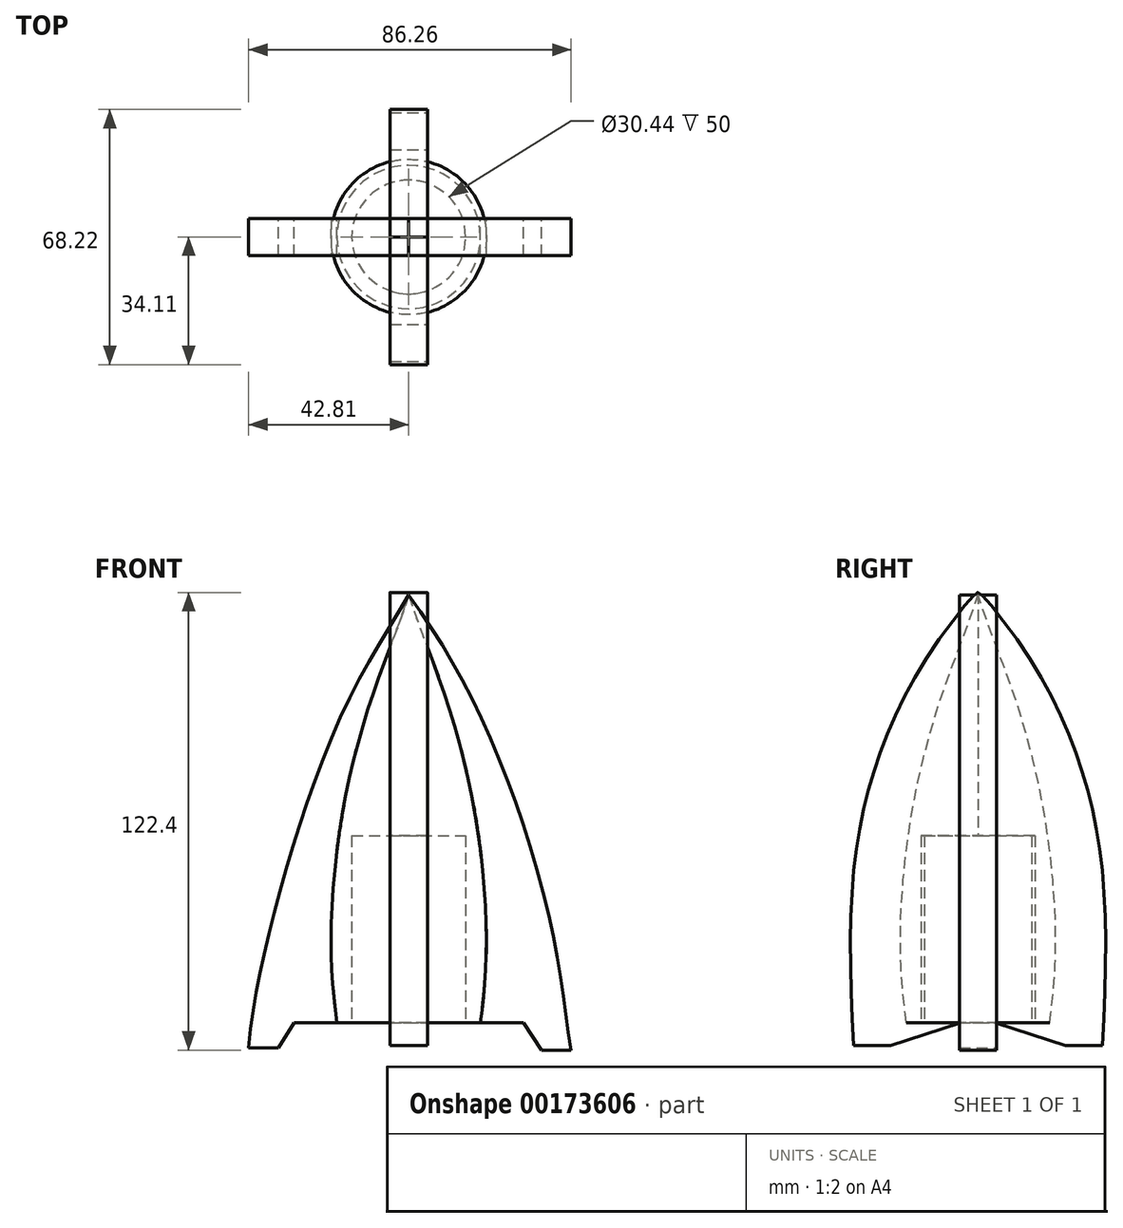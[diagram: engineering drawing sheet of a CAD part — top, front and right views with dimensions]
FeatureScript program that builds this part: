
annotation { "Feature Type Name" : "Feature", "Feature Type Description" : "" }
export const myFeature = defineFeature(function(context is Context, id is Id, definition is map)
    precondition{}
    {
        {
            var Q0;
            Q0=qCreatedBy(makeId("Front.planeOp"),FACE);
            var sketch = newSketch(context, id + "F0", { "sketchPlane" : qUnion([Q0])});
            skLineSegment(sketch, "E0", {"start": v(0, 52.55) * mm, "end": v(0, -61.82) * mm});
            skLineSegment(sketch, "E1", {"start": v(0, -61.82) * mm, "end": v(30.67, -61.82) * mm});
            skLineSegment(sketch, "E2", {"start": v(30.67, -61.82) * mm, "end": v(35.46, -69.17) * mm});
            skLineSegment(sketch, "E3", {"start": v(35.46, -69.17) * mm, "end": v(43.45, -69.17) * mm});
            skFitSpline(sketch, "E4", {"points": [v(0, 52.55) * mm, v(15.65, 27.31) * mm, v(29.71, -6.23) * mm, v(39.61, -43.6) * mm, v(43.45, -69.17) * mm], "startDerivative": vector(72.66, -100.15) * mm, "endDerivative": vector(20.38, -109.27) * mm});
            skFitSpline(sketch, "E5", {"points": [v(0, 52.55) * mm, v(9.26, 27) * mm, v(17.9, -6.87) * mm, v(20.77, -41.37) * mm, v(19.17, -61.82) * mm], "startDerivative": vector(32.35, -103.38) * mm, "endDerivative": vector(-11.58, -90.82) * mm});
            skFitSpline(sketch, "E6", {"points": [v(0, 52.55) * mm, v(-14.27, 28.11) * mm, v(-28.36, -6.5) * mm, v(-38.42, -42.32) * mm, v(-42.8, -68.53) * mm], "startDerivative": vector(-58.54, -99.73) * mm, "endDerivative": vector(-10.65, -116.82) * mm});
            skLineSegment(sketch, "E7", {"start": v(-42.8, -68.53) * mm, "end": v(-34.82, -68.53) * mm});
            skLineSegment(sketch, "E8", {"start": v(-34.82, -68.53) * mm, "end": v(-30.67, -61.82) * mm});
            skLineSegment(sketch, "E9", {"start": v(-30.67, -61.82) * mm, "end": v(0, -61.82) * mm});
            skFitSpline(sketch, "E10.MirrorCS", {"points": [v(0, 52.55) * mm, v(-9.26, 27) * mm, v(-17.9, -6.87) * mm, v(-20.77, -41.37) * mm, v(-19.17, -61.82) * mm], "startDerivative": vector(-32.35, -103.38) * mm, "endDerivative": vector(11.58, -90.82) * mm});
            skSolve(sketch);
        }
        {
            var Q0;
            {var subQ0=sQuery(id+"F0.wireOp",EDGE,"E0");Q0=makeQuery(id+"F0.imprint","IMPRINT",FACE,{"disambiguationData":[TD([[makeQuery(id+"F0.imprint","IMPRINT",EDGE,{"derivedFrom":subQ0}),1.0]])]});}
            var Q1;
            Q1=sQuery(id+"F0.wireOp",EDGE,"E0");
            revolve(context, id + "F1", {"entities" : qUnion([Q0]), "axis" : qUnion([Q1]), "revolveType" : RevolveType.FULL});
        }
        {
            var Q0;
            {var subQ0=sQuery(id+"F0.wireOp",EDGE,"E2");Q0=makeQuery(id+"F0.imprint","IMPRINT",FACE,{"disambiguationData":[TD([[makeQuery(id+"F0.imprint","IMPRINT",EDGE,{"derivedFrom":subQ0}),1.0]])]});}
            var Q1;
            Q1=makeQuery(id+"F0.imprint","IMPRINT",FACE,{"disambiguationData":[TD([[makeQuery(id+"F0.imprint","IMPRINT",EDGE,{"derivedFrom":sQuery(id+"F0.wireOp",EDGE,"E6")}),1.0]])]});
            extrude(context, id + "F2", {"entities" : qUnion([Q0, Q1]), "operationType" : NewBodyOperationType.ADD, "endBound" : BoundingType.SYMMETRIC, "depth" : 10 * mm});
        }
        {
            var Q0;
            Q0=qCreatedBy(makeId("Right.planeOp"),FACE);
            var sketch = newSketch(context, id + "F3", { "sketchPlane" : qUnion([Q0])});
            skLineSegment(sketch, "E11", {"start": v(-23.32, -67.89) * mm, "end": v(-33.23, -67.89) * mm});
            skFitSpline(sketch, "E12", {"points": [v(-33.23, -67.89) * mm, v(-33.23, -21.24) * mm, v(-26.84, 8.47) * mm, v(-12.14, 38.18) * mm, v(0, 53.2) * mm, v(0, 52.87) * mm], "startDerivative": vector(-10.45, 168.84) * mm, "endDerivative": vector(0, 0) * mm});
            skLineSegment(sketch, "E13", {"start": v(0, -60.4) * mm, "end": v(-23.32, -67.89) * mm});
            skLineSegment(sketch, "E14", {"start": v(0, 53.2) * mm, "end": v(0, -60.4) * mm});
            skSolve(sketch);
        }
        {
            var Q0;
            {var subQ5=sQuery(id+"F3.wireOp",EDGE,"E11");Q0=makeQuery(id+"F3.imprint","IMPRINT",FACE,{"disambiguationData":[TD([[makeQuery(id+"F3.imprint","IMPRINT",EDGE,{"derivedFrom":subQ5}),-1.0]])]});}
            extrude(context, id + "F4", {"entities" : qUnion([Q0]), "endBound" : BoundingType.SYMMETRIC, "oppositeDirection" : true, "depth" : 10 * mm});
        }
        {
            var Q0;
            Q0=makeQuery(id+"F4.opExtrude","SWEPT_BODY",BODY,{"disambiguationData":[OSD([sQuery(id+"F3.wireOp",EDGE,"E11"),sQuery(id+"F3.wireOp",EDGE,"E12"),sQuery(id+"F3.wireOp",EDGE,"E13"),sQuery(id+"F3.wireOp",EDGE,"E14")])]});
            var Q1;
            Q1=qCreatedBy(makeId("Front.planeOp"),FACE);
            mirror(context, id + "F5", {"entities" : qUnion([Q0]), "mirrorPlane" : qUnion([Q1])});
        }
        {
            var Q0;
            Q0=makeQuery(id+"F1.opRevolve","SWEPT_FACE",FACE,{"disambiguationData":[OSD([sQuery(id+"F0.wireOp",EDGE,"E1")])]});
            var sketch = newSketch(context, id + "F6", { "sketchPlane" : qUnion([Q0])});
            skCircle(sketch, "E15", {"center": v(0, 0) * mm, "radius": 15.22 * mm});
            skSolve(sketch);
        }
        {
            var Q0;
            Q0=makeQuery(id+"F6.imprint","IMPRINT",FACE,{"disambiguationData":[TD([[makeQuery(id+"F6.imprint","IMPRINT",EDGE,{"derivedFrom":sQuery(id+"F6.wireOp",EDGE,"E15")}),1.0]])]});
            var Q1;
            Q1=sQuery(id+"F6.wireOp",EDGE,"E15");
            extrude(context, id + "F7", {"entities" : qUnion([Q0]), "operationType" : NewBodyOperationType.REMOVE, "surfaceEntities" : qUnion([Q1]), "oppositeDirection" : true, "depth" : 50 * mm});
        }
    });
